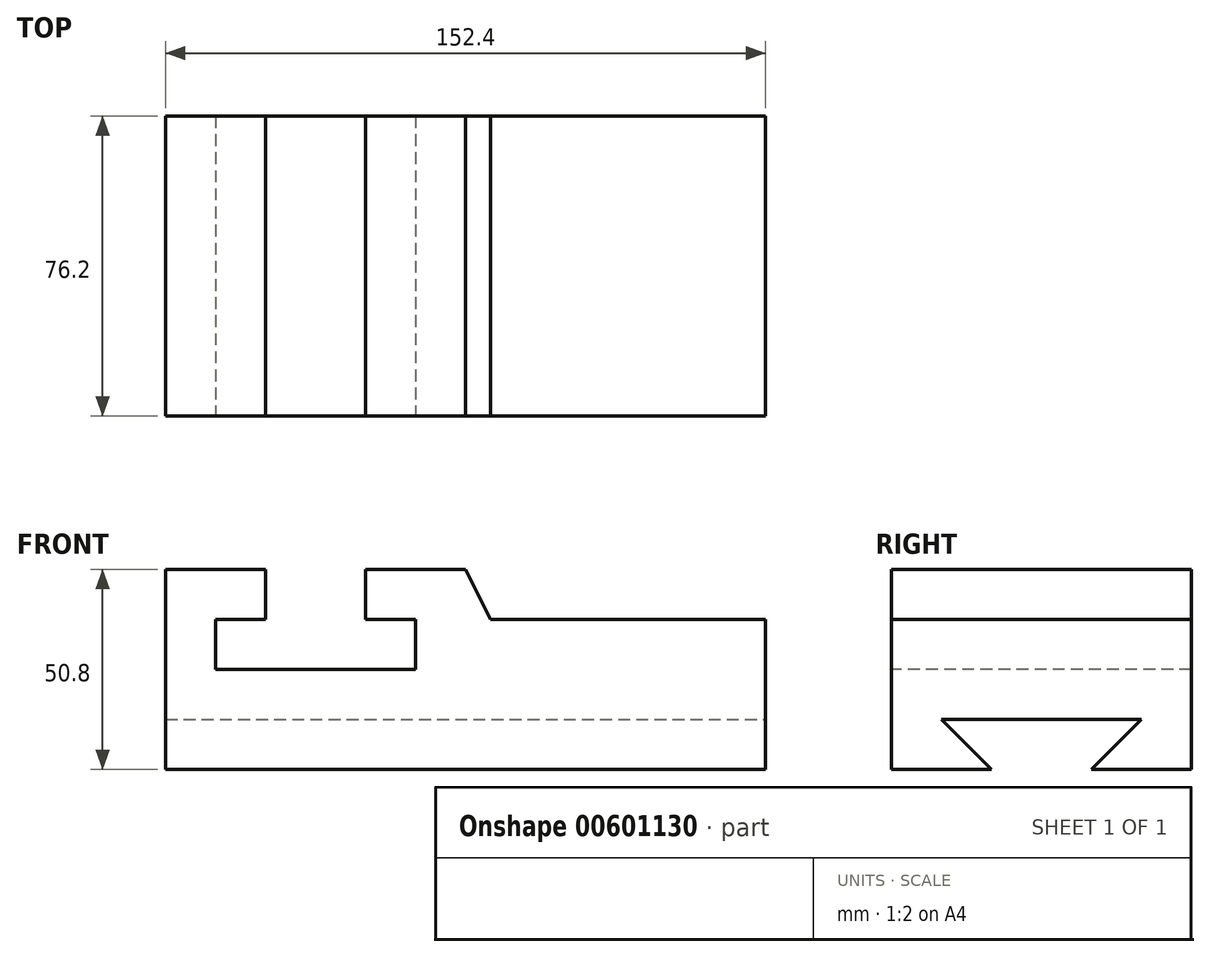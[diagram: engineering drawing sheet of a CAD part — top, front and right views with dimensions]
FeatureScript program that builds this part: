
annotation { "Feature Type Name" : "Feature", "Feature Type Description" : "" }
export const myFeature = defineFeature(function(context is Context, id is Id, definition is map)
    precondition{}
    {
        {
            var Q0;
            Q0=qCreatedBy(makeId("Front.planeOp"),FACE);
            var sketch = newSketch(context, id + "F0", { "sketchPlane" : qUnion([Q0])});
            skLineSegment(sketch, "E0", {"start": v(152.4, 0) * mm, "end": v(0, 0) * mm});
            skLineSegment(sketch, "E1", {"start": v(0, 0) * mm, "end": v(0, 50.8) * mm});
            skLineSegment(sketch, "E2", {"start": v(0, 50.8) * mm, "end": v(152.4, 50.8) * mm});
            skLineSegment(sketch, "E3", {"start": v(152.4, 50.8) * mm, "end": v(152.4, 0) * mm});
            skSolve(sketch);
        }
        {
            var Q0;
            Q0=makeQuery(id+"F0.imprint","IMPRINT",FACE,{"disambiguationData":[TD([[makeQuery(id+"F0.imprint","IMPRINT",EDGE,{"derivedFrom":sQuery(id+"F0.wireOp",EDGE,"E0")}),-1.0]])]});
            extrude(context, id + "F1", {"entities" : qUnion([Q0]), "oppositeDirection" : true, "depth" : 76.2 * mm, "offsetDistance" : 25.4 * mm});
        }
        {
            var Q0;
            Q0=makeQuery(id+"F1.opExtrude","SWEPT_FACE",FACE,{"disambiguationData":[OSD([sQuery(id+"F0.wireOp",EDGE,"E3")])]});
            var sketch = newSketch(context, id + "F2", { "sketchPlane" : qUnion([Q0])});
            skLineSegment(sketch, "E4", {"start": v(76.2, 0) * mm, "end": v(50.8, 0) * mm});
            skLineSegment(sketch, "E5", {"start": v(50.8, 0) * mm, "end": v(50.8, 12.7) * mm});
            skLineSegment(sketch, "E6", {"start": v(50.8, 12.7) * mm, "end": v(63.5, 12.7) * mm});
            skLineSegment(sketch, "E7", {"start": v(63.5, 12.7) * mm, "end": v(50.8, 0) * mm});
            skLineSegment(sketch, "E8", {"start": v(0, 0) * mm, "end": v(25.4, 0) * mm});
            skLineSegment(sketch, "E9", {"start": v(25.4, 0) * mm, "end": v(25.4, 12.7) * mm});
            skLineSegment(sketch, "E10", {"start": v(25.4, 12.7) * mm, "end": v(12.7, 12.7) * mm});
            skLineSegment(sketch, "E11", {"start": v(12.7, 12.7) * mm, "end": v(25.4, 0) * mm});
            skLineSegment(sketch, "E12", {"start": v(25.4, 12.7) * mm, "end": v(50.8, 12.7) * mm});
            skLineSegment(sketch, "E13", {"start": v(25.4, 0) * mm, "end": v(50.8, 0) * mm});
            skSolve(sketch);
        }
        {
            var Q0;
            Q0=makeQuery(id+"F2.imprint","IMPRINT",FACE,{"disambiguationData":[TD([[makeQuery(id+"F2.imprint","IMPRINT",EDGE,{"derivedFrom":sQuery(id+"F2.wireOp",EDGE,"E5")}),1.0]])]});
            var Q1;
            Q1=makeQuery(id+"F2.imprint","IMPRINT",FACE,{"disambiguationData":[TD([[makeQuery(id+"F2.imprint","IMPRINT",EDGE,{"derivedFrom":sQuery(id+"F2.wireOp",EDGE,"E9")}),1.0]])]});
            var Q2;
            Q2=makeQuery(id+"F2.imprint","IMPRINT",FACE,{"disambiguationData":[TD([[makeQuery(id+"F2.imprint","IMPRINT",EDGE,{"derivedFrom":sQuery(id+"F2.wireOp",EDGE,"E5")}),-1.0]])]});
            extrude(context, id + "F3", {"entities" : qUnion([Q0, Q1, Q2]), "operationType" : NewBodyOperationType.REMOVE, "oppositeDirection" : true, "depth" : 152.4 * mm, "offsetDistance" : 25.4 * mm});
        }
        {
            var Q0;
            Q0=makeQuery(id+"F1.opExtrude","CAP_FACE",FACE,{"disambiguationData":[OSD([sQuery(id+"F0.wireOp",EDGE,"E0"),sQuery(id+"F0.wireOp",EDGE,"E1"),sQuery(id+"F0.wireOp",EDGE,"E2"),sQuery(id+"F0.wireOp",EDGE,"E3")])],"isStart":true});
            var sketch = newSketch(context, id + "F4", { "sketchPlane" : qUnion([Q0])});
            skLineSegment(sketch, "E14", {"start": v(0, 50.8) * mm, "end": v(76.2, 50.8) * mm});
            skLineSegment(sketch, "E15", {"start": v(76.2, 50.8) * mm, "end": v(82.55, 50.8) * mm});
            skLineSegment(sketch, "E16", {"start": v(82.55, 50.8) * mm, "end": v(82.55, 38.1) * mm});
            skLineSegment(sketch, "E17", {"start": v(82.55, 38.1) * mm, "end": v(76.2, 50.8) * mm});
            skSolve(sketch);
        }
        {
            var Q0;
            Q0=makeQuery(id+"F4.imprint","IMPRINT",FACE,{"disambiguationData":[TD([[makeQuery(id+"F4.imprint","IMPRINT",EDGE,{"derivedFrom":sQuery(id+"F4.wireOp",EDGE,"E15")}),-1.0]])]});
            extrude(context, id + "F5", {"entities" : qUnion([Q0]), "operationType" : NewBodyOperationType.REMOVE, "oppositeDirection" : true, "depth" : 76.2 * mm, "offsetDistance" : 25.4 * mm});
        }
        {
            var Q0;
            Q0=makeQuery(id+"F1.opExtrude","CAP_FACE",FACE,{"disambiguationData":[OSD([sQuery(id+"F0.wireOp",EDGE,"E0"),sQuery(id+"F0.wireOp",EDGE,"E1"),sQuery(id+"F0.wireOp",EDGE,"E2"),sQuery(id+"F0.wireOp",EDGE,"E3")])],"isStart":true});
            var sketch = newSketch(context, id + "F6", { "sketchPlane" : qUnion([Q0])});
            skLineSegment(sketch, "E18", {"start": v(82.55, 38.1) * mm, "end": v(152.4, 38.1) * mm});
            skSolve(sketch);
        }
        {
            var Q0;
            {var subQ0=sQuery(id+"F6.wireOp",EDGE,"E18");Q0=makeQuery(id+"F6.imprint","IMPRINT",FACE,{"disambiguationData":[TD([[makeQuery(id+"F6.imprint","IMPRINT",EDGE,{"derivedFrom":subQ0}),1.0]])]});}
            extrude(context, id + "F7", {"entities" : qUnion([Q0]), "operationType" : NewBodyOperationType.REMOVE, "oppositeDirection" : true, "depth" : 76.2 * mm, "offsetDistance" : 25.4 * mm});
        }
        {
            var Q0;
            {var subQ1=sQuery(id+"F0.wireOp",EDGE,"E2");var subQ2=sQuery(id+"F0.wireOp",EDGE,"E1");Q0=makeQuery(id+"F5.boolean.opBoolean","SPLIT",FACE,{"disambiguationData":[TD([makeQuery(id+"F1.opExtrude","SWEPT_FACE",FACE,{"disambiguationData":[OSD([subQ2])]})])],"derivedFrom":makeQuery(id+"F1.opExtrude","SWEPT_FACE",FACE,{"disambiguationData":[OSD([subQ1])]})});}
            var sketch = newSketch(context, id + "F8", { "sketchPlane" : qUnion([Q0])});
            skLineSegment(sketch, "E19", {"start": v(25.4, 0) * mm, "end": v(25.4, 76.2) * mm});
            skLineSegment(sketch, "E20", {"start": v(25.4, 76.2) * mm, "end": v(50.8, 76.2) * mm});
            skLineSegment(sketch, "E21", {"start": v(50.8, 76.2) * mm, "end": v(50.8, 0) * mm});
            skLineSegment(sketch, "E22", {"start": v(50.8, 0) * mm, "end": v(25.4, 0) * mm});
            skSolve(sketch);
        }
        {
            var Q0;
            Q0=makeQuery(id+"F8.imprint","IMPRINT",FACE,{"disambiguationData":[TD([[makeQuery(id+"F8.imprint","IMPRINT",EDGE,{"derivedFrom":sQuery(id+"F8.wireOp",EDGE,"E19")}),-1.0]])]});
            extrude(context, id + "F9", {"entities" : qUnion([Q0]), "operationType" : NewBodyOperationType.REMOVE, "oppositeDirection" : true, "depth" : 25.4 * mm, "offsetDistance" : 25.4 * mm});
        }
        {
            var Q0;
            Q0=makeQuery(id+"F1.opExtrude","CAP_FACE",FACE,{"disambiguationData":[OSD([sQuery(id+"F0.wireOp",EDGE,"E0"),sQuery(id+"F0.wireOp",EDGE,"E1"),sQuery(id+"F0.wireOp",EDGE,"E2"),sQuery(id+"F0.wireOp",EDGE,"E3")])],"isStart":true});
            var sketch = newSketch(context, id + "F10", { "sketchPlane" : qUnion([Q0])});
            skLineSegment(sketch, "E23.bottom", {"start": v(50.8, 25.4) * mm, "end": v(63.5, 25.4) * mm});
            skLineSegment(sketch, "E23.top", {"start": v(50.8, 38.1) * mm, "end": v(63.5, 38.1) * mm});
            skLineSegment(sketch, "E23.left", {"start": v(50.8, 25.4) * mm, "end": v(50.8, 38.1) * mm});
            skLineSegment(sketch, "E23.right", {"start": v(63.5, 25.4) * mm, "end": v(63.5, 38.1) * mm});
            skLineSegment(sketch, "E24.bottom", {"start": v(25.4, 25.4) * mm, "end": v(12.7, 25.4) * mm});
            skLineSegment(sketch, "E24.top", {"start": v(25.4, 38.1) * mm, "end": v(12.7, 38.1) * mm});
            skLineSegment(sketch, "E24.left", {"start": v(25.4, 25.4) * mm, "end": v(25.4, 38.1) * mm});
            skLineSegment(sketch, "E24.right", {"start": v(12.7, 25.4) * mm, "end": v(12.7, 38.1) * mm});
            skSolve(sketch);
        }
        {
            var Q0;
            Q0=makeQuery(id+"F10.imprint","IMPRINT",FACE,{"disambiguationData":[TD([[makeQuery(id+"F10.imprint","IMPRINT",EDGE,{"derivedFrom":sQuery(id+"F10.wireOp",EDGE,"E24.bottom")}),-1.0]])]});
            var Q1;
            Q1=makeQuery(id+"F10.imprint","IMPRINT",FACE,{"disambiguationData":[TD([[makeQuery(id+"F10.imprint","IMPRINT",EDGE,{"derivedFrom":sQuery(id+"F10.wireOp",EDGE,"E23.bottom")}),1.0]])]});
            extrude(context, id + "F11", {"entities" : qUnion([Q0, Q1]), "operationType" : NewBodyOperationType.REMOVE, "oppositeDirection" : true, "depth" : 76.2 * mm, "offsetDistance" : 25.4 * mm});
        }
    });
